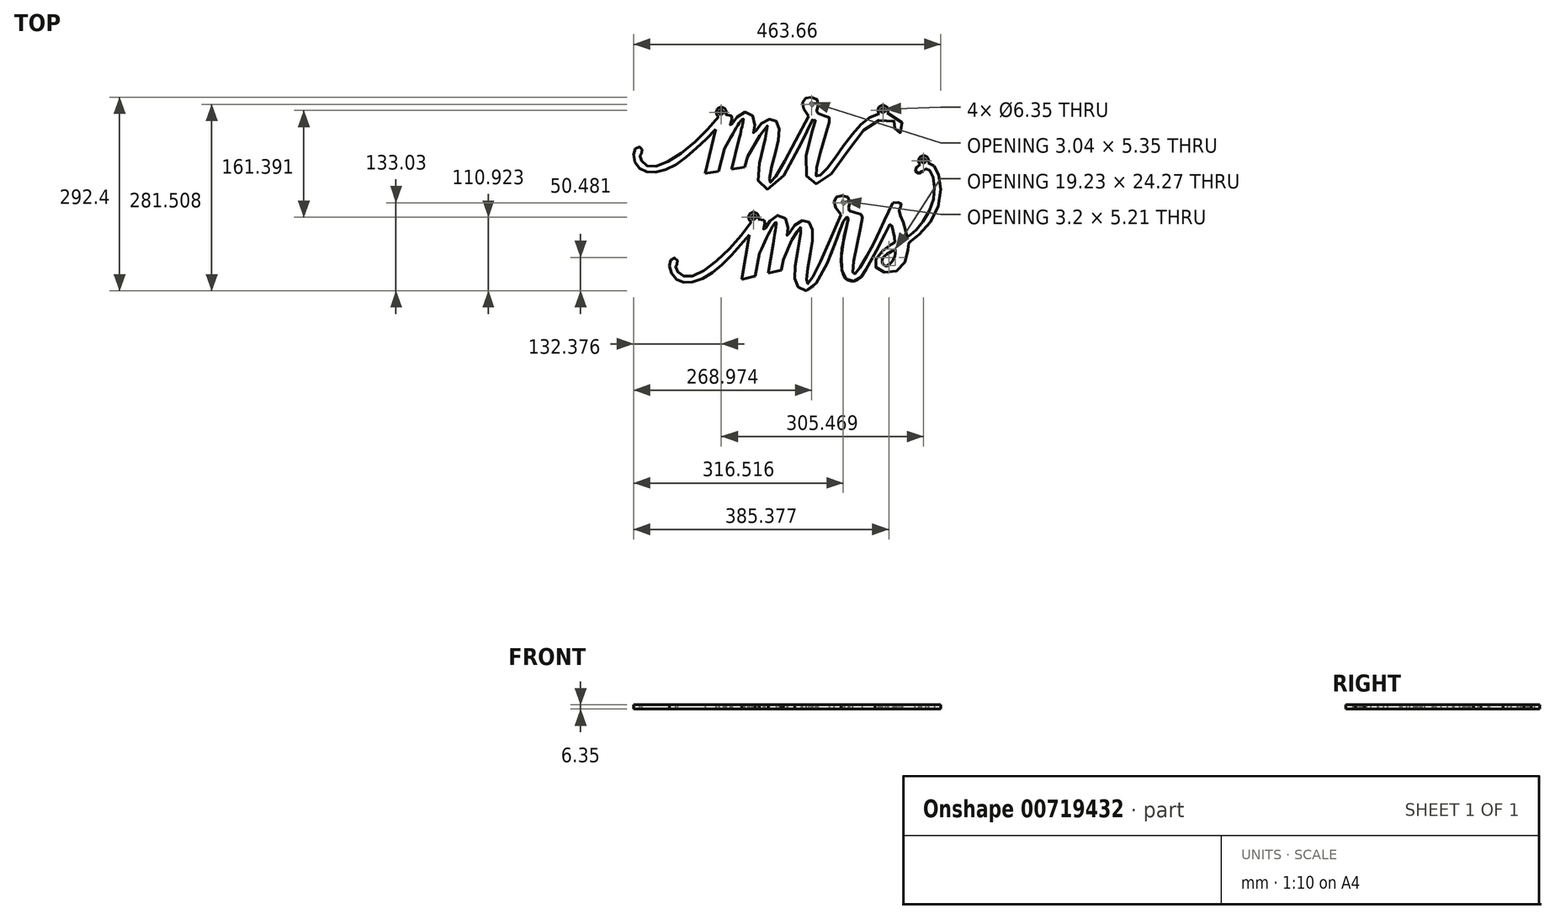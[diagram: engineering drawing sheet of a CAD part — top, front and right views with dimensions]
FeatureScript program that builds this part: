
annotation { "Feature Type Name" : "Feature", "Feature Type Description" : "" }
export const myFeature = defineFeature(function(context is Context, id is Id, definition is map)
    precondition{}
    {
        {
            var Q0;
            Q0=qCreatedBy(makeId("Top.planeOp"),FACE);
            var sketch = newSketch(context, id + "F0", { "sketchPlane" : qUnion([Q0])});
            skLineSegment(sketch, "E0", {"start": v(-227.64, 208.85) * mm, "end": v(178.76, 208.85) * mm});
            skLineSegment(sketch, "E1", {"start": v(-102.86, 97.91) * mm, "end": v(-119.08, 31.57) * mm});
            skLineSegment(sketch, "E2", {"start": v(-119.08, 31.57) * mm, "end": v(-98.57, 34.77) * mm});
            skLineSegment(sketch, "E3", {"start": v(-98.57, 34.77) * mm, "end": v(-89.6, 68.6) * mm});
            skLineSegment(sketch, "E4", {"start": v(-78.57, 38.02) * mm, "end": v(-67.8, 82.02) * mm});
            skLineSegment(sketch, "E5", {"start": v(-78.57, 38.02) * mm, "end": v(-58.82, 41.1) * mm});
            skLineSegment(sketch, "E6", {"start": v(-58.82, 41.1) * mm, "end": v(-54.63, 56.88) * mm});
            skFitSpline(sketch, "E7", {"points": [v(-89.6, 68.6) * mm, v(-63.3, 112.65) * mm, v(-61.33, 113.7) * mm, v(-61.48, 109.92) * mm, v(-67.8, 82.02) * mm], "startDerivative": vector(74.77, 142.63) * mm, "endDerivative": vector(-24.18, -98.88) * mm});
            skFitSpline(sketch, "E8", {"points": [v(-54.63, 56.88) * mm, v(-26.94, 101.34) * mm, v(-24.55, 103.27) * mm, v(-36.47, 48.66) * mm, v(-36.03, 14.66) * mm, v(-14.36, 10.7) * mm, v(43.41, 112.54) * mm, v(45.59, 113.3) * mm, v(47.48, 112.62) * mm, v(47.37, 109.52) * mm, v(35.3, 66.78) * mm, v(38.4, 19.73) * mm, v(59.88, 19.85) * mm, v(114.72, 90.21) * mm, v(151.17, 112.67) * mm, v(170.17, 106.45) * mm, v(167.07, 97.32) * mm, v(174.14, 91.65) * mm, v(179.29, 102.26) * mm, v(156.45, 123.02) * mm], "startDerivative": vector(435.53, 920) * mm, "endDerivative": vector(-919.75, 198.38) * mm});
            skFitSpline(sketch, "E9", {"points": [v(-102.86, 97.91) * mm, v(-176.7, 37.72) * mm, v(-218.96, 40.12) * mm, v(-225.18, 67.06) * mm, v(-216.17, 70.82) * mm, v(-214.34, 62.73) * mm, v(-217.4, 58.24) * mm, v(-202.78, 41.65) * mm, v(-98.41, 117.2) * mm], "startDerivative": vector(-316.02, -319.96) * mm, "endDerivative": vector(332.23, 430.61) * mm});
            skArc(sketch, "E10", {"start": v(-87.73, 120.14) * mm, "mid": v(-96.49, 131.06) * mm, "end": v(-98.41, 117.2) * mm});
            skFitSpline(sketch, "E11", {"points": [v(-87.73, 120.14) * mm, v(-78.78, 117.97) * mm, v(-77.26, 116.4) * mm, v(-80.6, 105.88) * mm, v(-80.47, 103.6) * mm, v(-77.97, 106.69) * mm, v(-60.08, 123.71) * mm, v(-43.73, 111.72) * mm, v(-45.98, 92.41) * mm, v(-45.05, 92.34) * mm, v(-33.92, 107.05) * mm, v(-15.05, 112.68) * mm, v(-7.08, 97.39) * mm, v(-16.24, 50.12) * mm, v(-21.44, 18.27) * mm, v(-19.44, 18.1) * mm, v(37.47, 117.88) * mm], "startDerivative": vector(229.22, -51.75) * mm, "endDerivative": vector(462.6, 877.17) * mm});
            skFitSpline(sketch, "E12", {"points": [v(37.47, 117.88) * mm, v(29.03, 140.17) * mm, v(38.21, 146.53) * mm, v(51.63, 140.4) * mm, v(49.44, 125.6) * mm, v(50.98, 122.52) * mm, v(67.17, 116.45) * mm, v(69.3, 112.76) * mm, v(48.5, 28.87) * mm, v(54.06, 27.62) * mm, v(97.7, 83.34) * mm, v(144.06, 121.35) * mm], "startDerivative": vector(-244.14, 268.34) * mm, "endDerivative": vector(345.92, 71.47) * mm});
            skFitSpline(sketch, "E13", {"points": [v(42.8, 133.03) * mm, v(40.91, 135.37) * mm, v(41.1, 138.32) * mm, v(43.52, 136.83) * mm, v(42.8, 133.03) * mm]});
            skArc(sketch, "E14", {"start": v(156.45, 123.02) * mm, "mid": v(148.65, 134.06) * mm, "end": v(144.06, 121.35) * mm});
            skCircle(sketch, "E15", {"center": v(-94.46, 123.71) * mm, "radius": 3.18 * mm});
            skCircle(sketch, "E16", {"center": v(149.67, 126.5) * mm, "radius": 3.18 * mm});
            skLineSegment(sketch, "E17", {"start": v(-52.06, -61.24) * mm, "end": v(-63.3, -128.6) * mm});
            skLineSegment(sketch, "E18", {"start": v(-63.3, -128.6) * mm, "end": v(-43.1, -123.89) * mm});
            skLineSegment(sketch, "E19", {"start": v(-43.1, -123.89) * mm, "end": v(-36.66, -89.48) * mm});
            skLineSegment(sketch, "E20", {"start": v(-23.39, -119.16) * mm, "end": v(-15.93, -74.49) * mm});
            skLineSegment(sketch, "E21", {"start": v(-23.39, -119.16) * mm, "end": v(-3.9, -114.62) * mm});
            skLineSegment(sketch, "E22", {"start": v(-3.9, -114.62) * mm, "end": v(-0.9, -98.6) * mm});
            skFitSpline(sketch, "E23", {"points": [v(-36.66, -89.48) * mm, v(-13.7, -43.6) * mm, v(-11.83, -42.41) * mm, v(-11.7, -46.18) * mm, v(-15.93, -74.49) * mm], "startDerivative": vector(63.95, 147.8) * mm, "endDerivative": vector(-16.76, -100.4) * mm});
            skFitSpline(sketch, "E24", {"points": [v(-0.9, -98.6) * mm, v(23.36, -52.23) * mm, v(25.74, -49.99) * mm, v(17.82, -105.42) * mm, v(20.77, -139.33) * mm, v(42.74, -141.66) * mm, v(92.64, -35.8) * mm, v(94.85, -34.8) * mm, v(96.87, -35.3) * mm, v(97, -38.61) * mm, v(87.93, -81.98) * mm, v(93.45, -127.62) * mm, v(110.7, -129.44) * mm, v(123.95, -114.2) * mm], "startDerivative": vector(365.86, 949.87) * mm, "endDerivative": vector(133.69, 224.75) * mm});
            skFitSpline(sketch, "E25", {"points": [v(-52.06, -61.24) * mm, v(-121.22, -126.76) * mm, v(-163.54, -127.51) * mm, v(-171.75, -101.1) * mm, v(-163.05, -96.69) * mm, v(-160.62, -104.63) * mm, v(-163.34, -109.33) * mm, v(-147.52, -124.79) * mm, v(-49.07, -41.68) * mm], "startDerivative": vector(-291.33, -342.6) * mm, "endDerivative": vector(299.26, 454.14) * mm});
            skArc(sketch, "E26", {"start": v(-38.64, -37.95) * mm, "mid": v(-48.18, -27.71) * mm, "end": v(-49.07, -41.68) * mm});
            skFitSpline(sketch, "E27", {"points": [v(-38.64, -37.95) * mm, v(-29.55, -39.44) * mm, v(-27.92, -40.9) * mm, v(-30.45, -51.64) * mm, v(-30.17, -53.9) * mm, v(-27.9, -50.64) * mm, v(-11.32, -32.33) * mm, v(5.87, -43.07) * mm, v(5.07, -62.5) * mm, v(6, -62.5) * mm, v(16, -47) * mm, v(34.4, -39.98) * mm, v(43.48, -54.64) * mm, v(37.87, -102.46) * mm, v(35.05, -134.6) * mm, v(37.06, -134.64) * mm, v(86.39, -30.9) * mm], "startDerivative": vector(232.43, -34.55) * mm, "endDerivative": vector(396.03, 909.16) * mm});
            skFitSpline(sketch, "E28", {"points": [v(86.39, -30.9) * mm, v(76.32, -9.29) * mm, v(85, -2.26) * mm, v(98.83, -7.37) * mm, v(97.75, -22.3) * mm, v(99.52, -25.25) * mm, v(116.11, -30.1) * mm, v(118.5, -33.62) * mm, v(104.01, -118.83) * mm, v(106.89, -120.47) * mm, v(142.59, -60.03) * mm, v(164.42, -12.9) * mm], "startDerivative": vector(-263.43, 249.43) * mm, "endDerivative": vector(163.33, 316.82) * mm});
            skFitSpline(sketch, "E29", {"points": [v(90.57, -15.39) * mm, v(88.52, -13.2) * mm, v(88.5, -10.23) * mm, v(91, -11.54) * mm, v(90.57, -15.39) * mm]});
            skCircle(sketch, "E30", {"center": v(-45.62, -34.89) * mm, "radius": 3.18 * mm});
            skFitSpline(sketch, "E31", {"points": [v(164.42, -12.9) * mm, v(176, -13.5) * mm, v(177.1, -17.17) * mm, v(174.06, -23.51) * mm, v(180.92, -44.88) * mm, v(185.95, -63.46) * mm, v(187.02, -63.92) * mm, v(190.78, -61.89) * mm, v(224.33, -13.99) * mm, v(220, 36.14) * mm, v(211.2, 36.88) * mm, v(203.93, 31.4) * mm, v(198.2, 36.46) * mm, v(205.72, 44.93) * mm], "startDerivative": vector(145.47, 31.12) * mm, "endDerivative": vector(101.53, 40) * mm});
            skFitSpline(sketch, "E32", {"points": [v(123.95, -114.2) * mm, v(161.12, -44.25) * mm, v(162.2, -44.41) * mm, v(167.6, -70.84) * mm, v(167.35, -72.79) * mm, v(165.36, -74.18) * mm, v(142.59, -92.17) * mm, v(140.73, -112.76) * mm, v(176.48, -111.86) * mm, v(188.01, -76.4) * mm, v(188.55, -73.56) * mm, v(190.76, -71.87) * mm, v(230.08, -26.62) * mm, v(229.34, 39.66) * mm, v(217.8, 46.99) * mm], "startDerivative": vector(383.8, 645.25) * mm, "endDerivative": vector(-168.67, 33.2) * mm});
            skFitSpline(sketch, "E33", {"points": [v(164.12, -85.26) * mm, v(149.4, -96.74) * mm, v(152.12, -108.1) * mm, v(165, -99.4) * mm, v(167.96, -83.68) * mm, v(167.16, -83.18) * mm, v(164.12, -85.26) * mm]});
            skArc(sketch, "E34", {"start": v(217.8, 46.99) * mm, "mid": v(209.73, 57.93) * mm, "end": v(205.72, 44.93) * mm});
            skCircle(sketch, "E35", {"center": v(211, 50.42) * mm, "radius": 3.18 * mm});
            skSolve(sketch);
        }
        {
            var Q0;
            Q0 = qSketchRegion(id + "F0", true);
            extrude(context, id + "F1", {"entities" : qUnion([Q0]), "depth" : 6.35 * mm, "offsetDistance" : 25.4 * mm});
        }
    });
